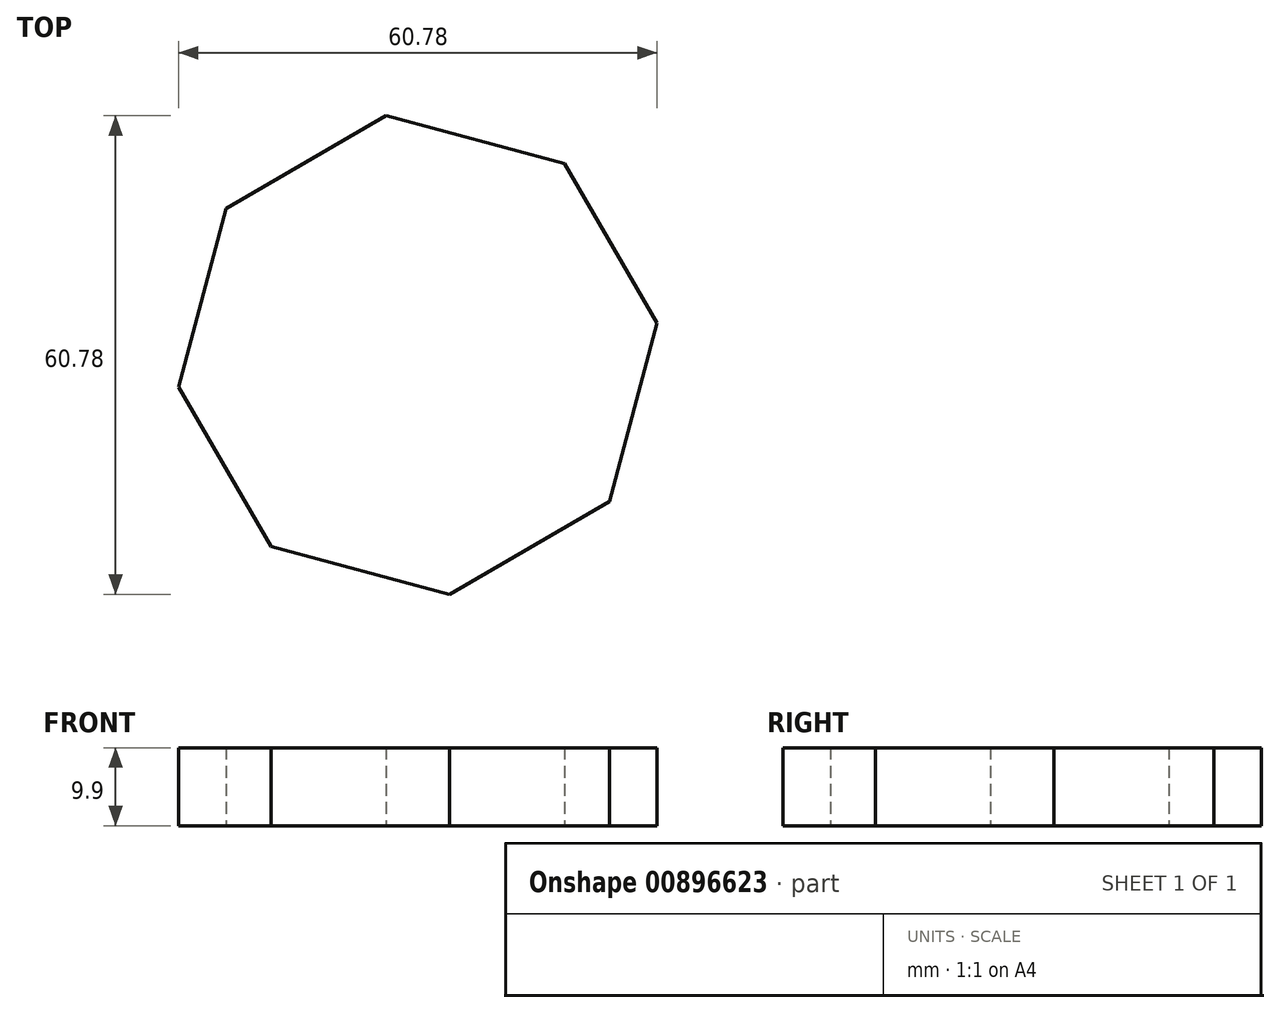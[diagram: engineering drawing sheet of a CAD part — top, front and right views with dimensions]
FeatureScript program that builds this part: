
annotation { "Feature Type Name" : "Feature", "Feature Type Description" : "" }
export const myFeature = defineFeature(function(context is Context, id is Id, definition is map)
    precondition{}
    {
        {
            var Q0;
            Q0=qCreatedBy(makeId("Top.planeOp"),FACE);
            var sketch = newSketch(context, id + "F0", { "sketchPlane" : qUnion([Q0])});
            skCircle(sketch, "E0.cCircle", {"center": v(0, 0) * mm, "radius": 28.32 * mm, "construction": true});
            skLineSegment(sketch, "E0.0", {"start": v(-18.63, -24.35) * mm, "end": v(-30.4, -4.04) * mm});
            skLineSegment(sketch, "E0.1", {"start": v(-30.4, -4.04) * mm, "end": v(-24.35, 18.63) * mm});
            skLineSegment(sketch, "E0.2", {"start": v(-24.35, 18.63) * mm, "end": v(-4.04, 30.4) * mm});
            skLineSegment(sketch, "E0.3", {"start": v(-4.04, 30.4) * mm, "end": v(18.63, 24.35) * mm});
            skLineSegment(sketch, "E0.4", {"start": v(18.63, 24.35) * mm, "end": v(30.4, 4.04) * mm});
            skLineSegment(sketch, "E0.5", {"start": v(30.4, 4.04) * mm, "end": v(24.35, -18.63) * mm});
            skLineSegment(sketch, "E0.6", {"start": v(24.35, -18.63) * mm, "end": v(4.04, -30.4) * mm});
            skLineSegment(sketch, "E0.7", {"start": v(4.04, -30.4) * mm, "end": v(-18.63, -24.35) * mm});
            skPoint(sketch, "E0.0.midPoint", {"position": v(-24.51, -14.2) * mm});
            skSolve(sketch);
        }
        {
            var Q0;
            Q0=makeQuery(id+"F0.imprint","IMPRINT",FACE,{"disambiguationData":[TD([[makeQuery(id+"F0.imprint","IMPRINT",EDGE,{"derivedFrom":sQuery(id+"F0.wireOp",EDGE,"E0.0")}),-1.0]])]});
            extrude(context, id + "F1", {"entities" : qUnion([Q0]), "depth" : 9.9 * mm, "offsetDistance" : 25 * mm});
        }
    });
